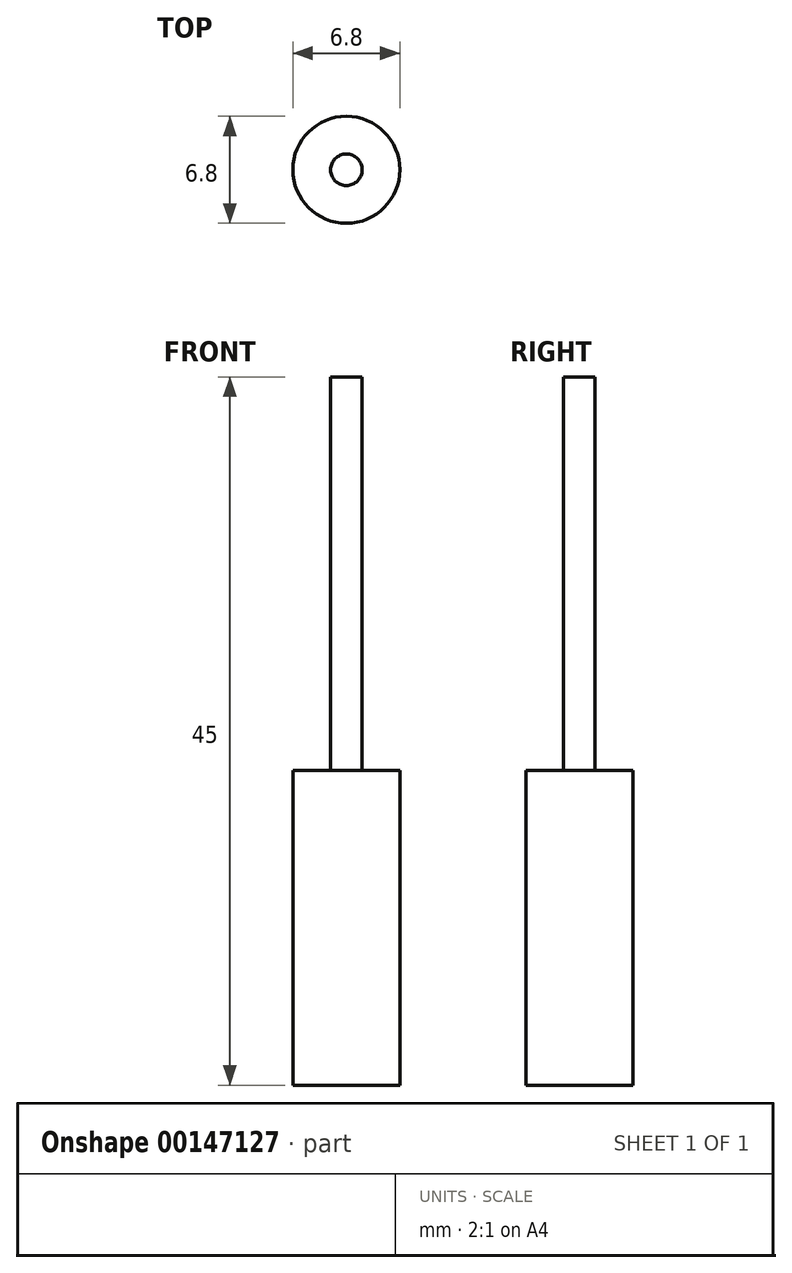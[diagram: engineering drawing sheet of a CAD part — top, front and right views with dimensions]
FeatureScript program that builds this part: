
annotation { "Feature Type Name" : "Feature", "Feature Type Description" : "" }
export const myFeature = defineFeature(function(context is Context, id is Id, definition is map)
    precondition{}
    {
        {
            var Q0;
            Q0=qCreatedBy(makeId("Top.planeOp"),FACE);
            var sketch = newSketch(context, id + "F0", { "sketchPlane" : qUnion([Q0])});
            skPoint(sketch, "E0.middle", {"position": v(0, 0) * mm});
            skCircle(sketch, "E1", {"center": v(0, 0) * mm, "radius": 3.4 * mm});
            skCircle(sketch, "E2", {"center": v(0, 0) * mm, "radius": 1 * mm});
            skSolve(sketch);
        }
        {
            var Q0;
            Q0=qSketchRegion(id+"F0",true);
            var Q1;
            Q1=makeQuery(id+"F0.imprint","IMPRINT",FACE,{"disambiguationData":[TD([[makeQuery(id+"F0.imprint","IMPRINT",EDGE,{"derivedFrom":sQuery(id+"F0.wireOp",EDGE,"uYGc6gbQ-b4I5-IUv8-2ImV-eN4ShZYCs7Or.bottom")}),1.0]])]});
            var Q2;
            Q2=makeQuery(id+"F0.imprint","IMPRINT",FACE,{"disambiguationData":[TD([[makeQuery(id+"F0.imprint","IMPRINT",EDGE,{"derivedFrom":sQuery(id+"F0.wireOp",EDGE,"g2bdyTXF-R3BZ-33Fl-nZeH-LAzpeJCssf24")}),1.0]])]});
            var Q3;
            Q3=makeQuery(id+"F0.imprint","IMPRINT",FACE,{"disambiguationData":[TD([[makeQuery(id+"F0.imprint","IMPRINT",EDGE,{"derivedFrom":sQuery(id+"F0.wireOp",EDGE,"E2")}),1.0]])]});
            extrude(context, id + "F1", {"entities" : qUnion([Q0, Q1, Q2, Q3]), "oppositeDirection" : true, "depth" : 20 * mm});
        }
        {
            var Q0;
            Q0=makeQuery(id+"F0.imprint","IMPRINT",FACE,{"disambiguationData":[TD([[makeQuery(id+"F0.imprint","IMPRINT",EDGE,{"derivedFrom":sQuery(id+"F0.wireOp",EDGE,"E2")}),1.0]])]});
            extrude(context, id + "F2", {"entities" : qUnion([Q0]), "depth" : 25 * mm});
        }
    });
